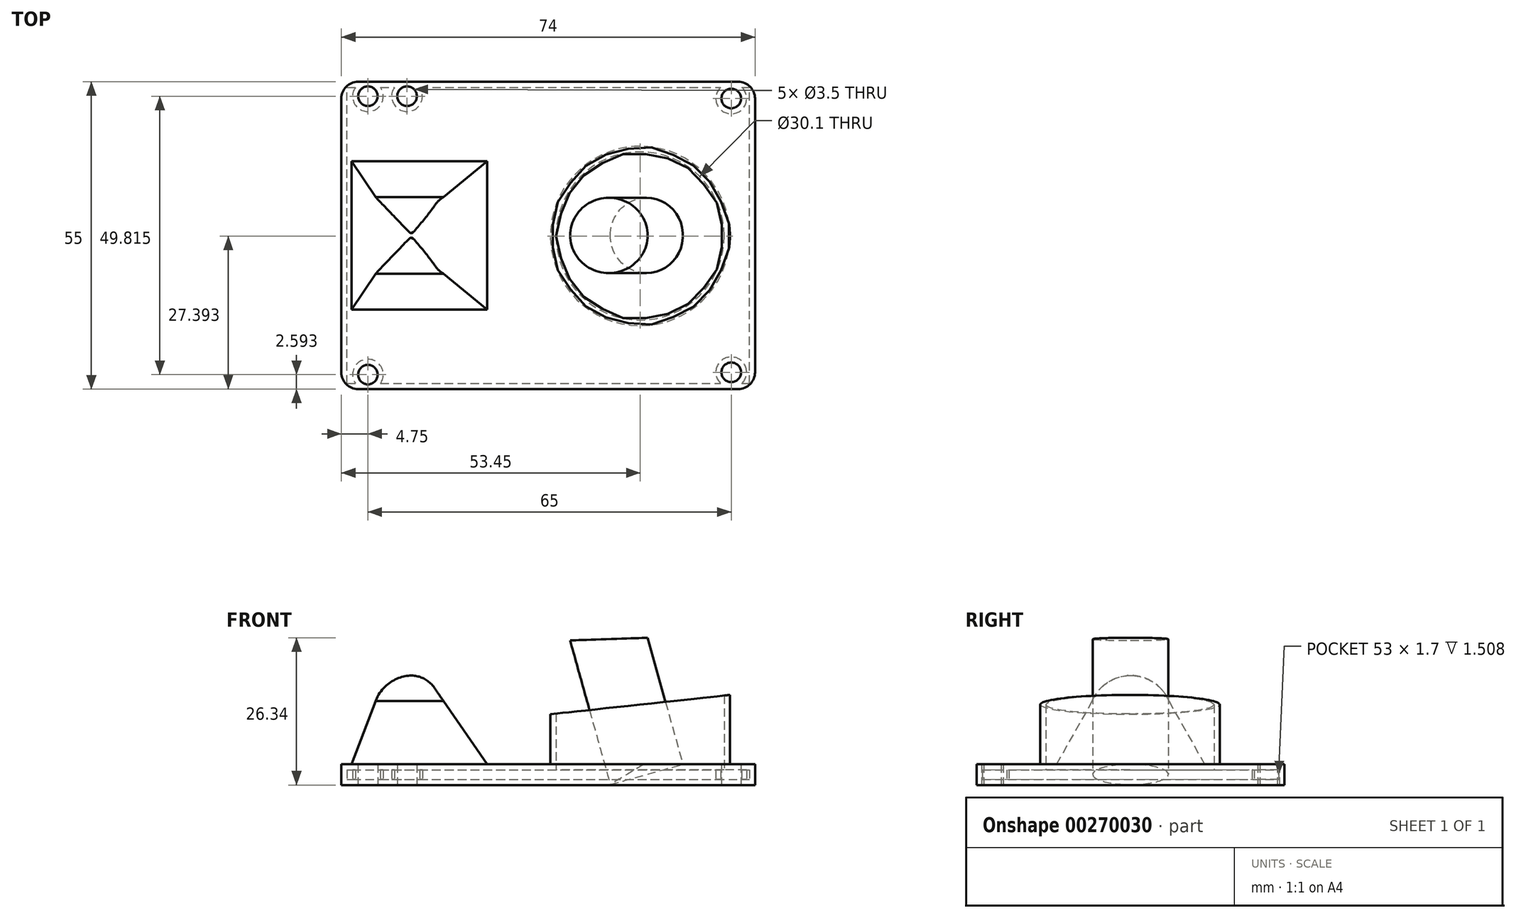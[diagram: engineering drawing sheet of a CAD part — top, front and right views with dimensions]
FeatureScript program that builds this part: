
annotation { "Feature Type Name" : "Feature", "Feature Type Description" : "" }
export const myFeature = defineFeature(function(context is Context, id is Id, definition is map)
    precondition{}
    {
        {
            var Q0;
            Q0=qCreatedBy(makeId("Top.planeOp"),FACE);
            var sketch = newSketch(context, id + "F0", { "sketchPlane" : qUnion([Q0])});
            skLineSegment(sketch, "E0.bottom", {"start": v(-37, -27.5) * mm, "end": v(37, -27.5) * mm});
            skLineSegment(sketch, "E0.top", {"start": v(-37, 27.5) * mm, "end": v(37, 27.5) * mm});
            skLineSegment(sketch, "E0.left", {"start": v(-37, -27.5) * mm, "end": v(-37, 27.5) * mm});
            skLineSegment(sketch, "E0.right", {"start": v(37, -27.5) * mm, "end": v(37, 27.5) * mm});
            skPoint(sketch, "E0.middle", {"position": v(0, 0) * mm});
            skPoint(sketch, "E1.endSnap0", {"position": v(37, 0) * mm});
            skPoint(sketch, "E2.endSnap0", {"position": v(-37, 0) * mm});
            skLineSegment(sketch, "E3.bottom", {"start": v(-35.85, -13) * mm, "end": v(-5.85, -13) * mm});
            skLineSegment(sketch, "E3.top", {"start": v(-35.85, 13) * mm, "end": v(-5.85, 13) * mm});
            skLineSegment(sketch, "E3.left", {"start": v(-35.85, -13) * mm, "end": v(-35.85, 13) * mm});
            skLineSegment(sketch, "E3.right", {"start": v(-5.85, -13) * mm, "end": v(-5.85, 13) * mm});
            skPoint(sketch, "E3.middle", {"position": v(-20.85, 0) * mm});
            skCircle(sketch, "E4.MirrorC", {"center": v(-32.25, 24.9) * mm, "radius": 1.75 * mm});
            skCircle(sketch, "E5.MirrorC", {"center": v(32.75, 24.5) * mm, "radius": 1.75 * mm});
            skCircle(sketch, "E6.MirrorC", {"center": v(-25.25, 24.9) * mm, "radius": 1.75 * mm});
            skCircle(sketch, "E7", {"center": v(16.45, -0.1) * mm, "radius": 16.05 * mm});
            skCircle(sketch, "E8.MirrorC", {"center": v(-32.25, -24.9) * mm, "radius": 1.75 * mm});
            skCircle(sketch, "E9.MirrorC", {"center": v(32.75, -24.5) * mm, "radius": 1.75 * mm});
            skSolve(sketch);
        }
        {
            var Q0;
            {var subQ1=sQuery(id+"F0.wireOp",EDGE,"E0.bottom");Q0=makeQuery(id+"F0.imprint","IMPRINT",FACE,{"disambiguationData":[TD([[makeQuery(id+"F0.imprint","IMPRINT",EDGE,{"derivedFrom":subQ1}),1.0]])]});}
            var Q1;
            Q1=makeQuery(id+"F0.imprint","IMPRINT",FACE,{"disambiguationData":[TD([[makeQuery(id+"F0.imprint","IMPRINT",EDGE,{"derivedFrom":sQuery(id+"F0.wireOp",EDGE,"E7")}),1.0]])]});
            var Q2;
            {var subQ5=sQuery(id+"F0.wireOp",EDGE,"E3.top");Q2=makeQuery(id+"F0.imprint","IMPRINT",FACE,{"disambiguationData":[TD([[makeQuery(id+"F0.imprint","IMPRINT",EDGE,{"derivedFrom":subQ5}),-1.0]])]});}
            var Q3;
            {var subQ5=sQuery(id+"F0.wireOp",EDGE,"E3.bottom");Q3=makeQuery(id+"F0.imprint","IMPRINT",FACE,{"disambiguationData":[TD([[makeQuery(id+"F0.imprint","IMPRINT",EDGE,{"derivedFrom":subQ5}),1.0]])]});}
            extrude(context, id + "F1", {"entities" : qUnion([Q0, Q1, Q2, Q3]), "depth" : 3.7 * mm});
        }
        {
            var Q0;
            Q0=makeQuery(id+"F0.imprint","IMPRINT",FACE,{"disambiguationData":[TD([[makeQuery(id+"F0.imprint","IMPRINT",EDGE,{"derivedFrom":sQuery(id+"F0.wireOp",EDGE,"E7")}),1.0]])]});
            extrude(context, id + "F2", {"entities" : qUnion([Q0]), "operationType" : NewBodyOperationType.ADD, "depth" : 16.1 * mm});
        }
        {
            var Q0;
            Q0=makeQuery(id+"F2.opExtrude","CAP_FACE",FACE,{"disambiguationData":[OSD([sQuery(id+"F0.wireOp",EDGE,"E7")])],"isStart":false});
            shell(context, id + "F3", {"entities" : qUnion([Q0]), "thickness" : 1 * mm});
        }
        {
            var Q0;
            Q0=makeQuery(id+"F1.opExtrude","SWEPT_EDGE",EDGE,{"disambiguationData":[OSD([sQuery(id+"F0.wireOp",EDGE,"E0.bottom"),sQuery(id+"F0.wireOp",EDGE,"E0.right")])]});
            fillet(context, id + "F4", {"entities" : qUnion([Q0]), "radius" : 3 * mm, "tangentPropagation" : true, "allowEdgeOverflow" : false});
        }
        {
            var Q0;
            Q0=makeQuery(id+"F1.opExtrude","SWEPT_EDGE",EDGE,{"disambiguationData":[OSD([sQuery(id+"F0.wireOp",EDGE,"E0.bottom"),sQuery(id+"F0.wireOp",EDGE,"E0.left")])]});
            fillet(context, id + "F5", {"entities" : qUnion([Q0]), "radius" : 3 * mm, "tangentPropagation" : true, "allowEdgeOverflow" : false});
        }
        {
            var Q0;
            Q0=makeQuery(id+"F1.opExtrude","SWEPT_EDGE",EDGE,{"disambiguationData":[OSD([sQuery(id+"F0.wireOp",EDGE,"E0.top"),sQuery(id+"F0.wireOp",EDGE,"E0.right")])]});
            var Q1;
            Q1=makeQuery(id+"F1.opExtrude","SWEPT_EDGE",EDGE,{"disambiguationData":[OSD([sQuery(id+"F0.wireOp",EDGE,"E0.top"),sQuery(id+"F0.wireOp",EDGE,"E0.left")])]});
            fillet(context, id + "F6", {"entities" : qUnion([Q0, Q1]), "radius" : 3 * mm, "tangentPropagation" : true, "allowEdgeOverflow" : false});
        }
        {
            var Q0;
            Q0=qCreatedBy(makeId("Front.planeOp"),FACE);
            var sketch = newSketch(context, id + "F7", { "sketchPlane" : qUnion([Q0])});
            skLineSegment(sketch, "E10", {"start": v(32.79, 0) * mm, "end": v(32.79, 16.15) * mm});
            skLineSegment(sketch, "E11", {"start": v(32.79, 16.15) * mm, "end": v(0.29, 16.15) * mm});
            skLineSegment(sketch, "E12", {"start": v(0.29, 16.15) * mm, "end": v(0.29, 12.65) * mm});
            skLineSegment(sketch, "E13", {"start": v(0.29, 12.65) * mm, "end": v(32.79, 16.15) * mm});
            skSolve(sketch);
        }
        {
            var Q0;
            Q0 = qSketchRegion(id + "F7", true);
            extrude(context, id + "F8", {"entities" : qUnion([Q0]), "operationType" : NewBodyOperationType.REMOVE, "oppositeDirection" : true, "depth" : 25 * mm, "hasSecondDirection" : true, "secondDirectionOppositeDirection" : false, "secondDirectionDepth" : 25 * mm});
        }
        {
            var Q0;
            Q0=qCreatedBy(makeId("Front.planeOp"),FACE);
            var sketch = newSketch(context, id + "F9", { "sketchPlane" : qUnion([Q0])});
            skLineSegment(sketch, "E14.0", {"start": v(-34, 3.7) * mm, "end": v(-10.92, 3.7) * mm});
            skLineSegment(sketch, "E15", {"start": v(-10.92, 3.7) * mm, "end": v(-21.48, 19) * mm});
            skLineSegment(sketch, "E16", {"start": v(-35.2, 3.7) * mm, "end": v(-30.84, 15.08) * mm});
            skArc(sketch, "E17", {"start": v(-30.84, 15.08) * mm, "mid": v(-27, 19.05) * mm, "end": v(-21.48, 19) * mm});
            skPoint(sketch, "E18.orphan", {"position": v(34, 3.7) * mm});
            skLineSegment(sketch, "E19", {"start": v(-35.2, 3.7) * mm, "end": v(-10.92, 3.7) * mm});
            skSolve(sketch);
        }
        {
            var Q0;
            {var subQ0=sQuery(id+"F9.wireOp",EDGE,"E15");Q0=makeQuery(id+"F9.imprint","IMPRINT",FACE,{"disambiguationData":[TD([[makeQuery(id+"F9.imprint","IMPRINT",EDGE,{"derivedFrom":subQ0}),1.0]])]});}
            extrude(context, id + "F10", {"entities" : qUnion([Q0]), "operationType" : NewBodyOperationType.ADD, "endBound" : BoundingType.SYMMETRIC, "depth" : 26.5 * mm});
        }
        {
            var Q0;
            Q0=qCreatedBy(makeId("Right.planeOp"),FACE);
            var sketch = newSketch(context, id + "F11", { "sketchPlane" : qUnion([Q0])});
            skLineSegment(sketch, "E20.0", {"start": v(13.25, 15.08) * mm, "end": v(13.25, 19.59) * mm});
            skLineSegment(sketch, "E20.1", {"start": v(13.25, 3.7) * mm, "end": v(13.25, 15.08) * mm});
            skLineSegment(sketch, "E20.2", {"start": v(-13.25, 15.08) * mm, "end": v(-13.25, 19.59) * mm});
            skLineSegment(sketch, "E20.3", {"start": v(-13.25, 3.7) * mm, "end": v(-13.25, 15.08) * mm});
            skLineSegment(sketch, "E20.4", {"start": v(-24.5, 3.7) * mm, "end": v(24.5, 3.7) * mm});
            skLineSegment(sketch, "E20.5.0", {"start": v(13.25, 19.59) * mm, "end": v(13.25, 15.08) * mm});
            skLineSegment(sketch, "E20.5.2", {"start": v(-13.25, 15.08) * mm, "end": v(-13.25, 19.59) * mm});
            skLineSegment(sketch, "E21", {"start": v(0, 19) * mm, "end": v(0, 3.7) * mm, "construction": true});
            skLineSegment(sketch, "E22", {"start": v(13.25, 3.7) * mm, "end": v(6.87, 15.03) * mm});
            skLineSegment(sketch, "E23.MirrorCS", {"start": v(-13.25, 3.7) * mm, "end": v(-6.87, 15.03) * mm});
            skLineSegment(sketch, "E24", {"start": v(13.25, 19.59) * mm, "end": v(-13.25, 19.59) * mm});
            skArc(sketch, "E25", {"start": v(6.87, 15.03) * mm, "mid": v(0, 19.59) * mm, "end": v(-6.87, 15.03) * mm});
            skLineSegment(sketch, "E26", {"start": v(13.25, 3.7) * mm, "end": v(-13.25, 3.7) * mm});
            skSolve(sketch);
        }
        {
            var Q0;
            Q0=makeQuery(id+"F11.imprint","IMPRINT",FACE,{"disambiguationData":[TD([[makeQuery(id+"F11.imprint","IMPRINT",EDGE,{"derivedFrom":sQuery(id+"F11.wireOp",EDGE,"E20.3")}),-1.0]])]});
            var Q1;
            Q1=makeQuery(id+"F11.imprint","IMPRINT",FACE,{"disambiguationData":[TD([[makeQuery(id+"F11.imprint","IMPRINT",EDGE,{"derivedFrom":sQuery(id+"F11.wireOp",EDGE,"E20.1")}),1.0]])]});
            extrude(context, id + "F12", {"entities" : qUnion([Q0, Q1]), "operationType" : NewBodyOperationType.REMOVE, "oppositeDirection" : true, "depth" : 45 * mm});
        }
        {
            var Q0;
            Q0=makeQuery(id+"F10.opExtrude","SWEPT_EDGE",EDGE,{"disambiguationData":[OSD([sQuery(id+"F9.wireOp",EDGE,"E15"),sQuery(id+"F9.wireOp",EDGE,"E17")])]});
            fillet(context, id + "F13", {"entities" : qUnion([Q0]), "radius" : 5 * mm, "tangentPropagation" : true, "allowEdgeOverflow" : false});
        }
        {
            var Q0;
            Q0=qCreatedBy(makeId("Top.planeOp"),FACE);
            var sketch = newSketch(context, id + "F14", { "sketchPlane" : qUnion([Q0])});
            skCircle(sketch, "E27.0", {"center": v(-32.25, 24.9) * mm, "radius": 1.75 * mm});
            skCircle(sketch, "E28.0", {"center": v(-25.25, 24.9) * mm, "radius": 1.75 * mm});
            skSolve(sketch);
        }
        {
            var Q0;
            Q0=makeQuery(id+"F14.imprint","IMPRINT",FACE,{"disambiguationData":[TD([[makeQuery(id+"F14.imprint","IMPRINT",EDGE,{"derivedFrom":sQuery(id+"F14.wireOp",EDGE,"E27.0")}),1.0]])]});
            var Q1;
            Q1=makeQuery(id+"F14.imprint","IMPRINT",FACE,{"disambiguationData":[TD([[makeQuery(id+"F14.imprint","IMPRINT",EDGE,{"derivedFrom":sQuery(id+"F14.wireOp",EDGE,"E28.0")}),1.0]])]});
            extrude(context, id + "F15", {"entities" : qUnion([Q0, Q1]), "operationType" : NewBodyOperationType.REMOVE, "endBound" : BoundingType.THROUGH_ALL, "oppositeDirection" : true, "depth" : 25 * mm});
        }
        {
            var Q0;
            Q0=qCreatedBy(makeId("Front.planeOp"),FACE);
            var sketch = newSketch(context, id + "F16", { "sketchPlane" : qUnion([Q0])});
            skLineSegment(sketch, "E29", {"start": v(0.4, 3.7) * mm, "end": v(0.4, 12.66) * mm});
            skLineSegment(sketch, "E30", {"start": v(32.5, 16.1) * mm, "end": v(32.5, 3.7) * mm});
            skLineSegment(sketch, "E31", {"start": v(17.1, 3.7) * mm, "end": v(9.78, 29.97) * mm});
            skLineSegment(sketch, "E32", {"start": v(9.78, 29.97) * mm, "end": v(16.78, 29.97) * mm});
            skLineSegment(sketch, "E33", {"start": v(16.78, 29.97) * mm, "end": v(24.1, 3.7) * mm});
            skLineSegment(sketch, "E34", {"start": v(24.1, 3.7) * mm, "end": v(17.1, 3.7) * mm});
            skSolve(sketch);
        }
        {
            var Q0;
            Q0 = qSketchRegion(id + "F16", true);
            var Q1;
            Q1=sQuery(id+"F16.wireOp",EDGE,"E31");
            revolve(context, id + "F17", {"entities" : qUnion([Q0]), "axis" : qUnion([Q1]), "revolveType" : RevolveType.FULL});
        }
        {
            var Q0;
            Q0=qCreatedBy(makeId("Front.planeOp"),FACE);
            var sketch = newSketch(context, id + "F18", { "sketchPlane" : qUnion([Q0])});
            skLineSegment(sketch, "E35", {"start": v(11, 0.48) * mm, "end": v(3.92, 25.87) * mm});
            skLineSegment(sketch, "E36", {"start": v(16.92, 29.45) * mm, "end": v(24.24, 3.18) * mm});
            skLineSegment(sketch, "E37", {"start": v(3.92, 25.87) * mm, "end": v(17.79, 26.34) * mm});
            skLineSegment(sketch, "E38", {"start": v(17.79, 26.34) * mm, "end": v(18.23, 32.35) * mm});
            skLineSegment(sketch, "E39", {"start": v(18.23, 32.35) * mm, "end": v(4.99, 32.76) * mm});
            skLineSegment(sketch, "E40", {"start": v(3.92, 25.87) * mm, "end": v(0.28, 25.74) * mm});
            skLineSegment(sketch, "E41", {"start": v(0.28, 25.74) * mm, "end": v(2.06, 32.88) * mm});
            skLineSegment(sketch, "E42", {"start": v(2.06, 32.88) * mm, "end": v(4.99, 32.76) * mm});
            skSolve(sketch);
        }
        {
            var Q0;
            Q0=makeQuery(id+"F18.imprint","IMPRINT",FACE,{"disambiguationData":[TD([[makeQuery(id+"F18.imprint","IMPRINT",EDGE,{"derivedFrom":sQuery(id+"F18.wireOp",EDGE,"E37")}),1.0]])]});
            extrude(context, id + "F19", {"entities" : qUnion([Q0]), "operationType" : NewBodyOperationType.REMOVE, "endBound" : BoundingType.SYMMETRIC, "oppositeDirection" : true, "depth" : 25 * mm});
        }
    });
